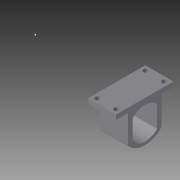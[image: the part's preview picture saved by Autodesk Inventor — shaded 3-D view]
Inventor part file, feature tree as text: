
AUTODESK INVENTOR PART (.ipt)
format: ipt  version: 2015 (Build 190159000, 159)  size: 276,480 bytes
history: native  units: in
note: dims shown in document units (in); Inventor stores cm internally (conversion verified against a paired STEP export)
features: sketch x21, extrude x20, fillet x2, plane x1, pattern_circular x1, mirror x1
ambient origin geometry x8: Origin, YZ Plane, XZ Plane, XY Plane, X Axis, Y Axis, Z Axis, Center Point
bodies: Solid1 (feature_tree)
feature tree (46):
  extrude  "Extrusion1"  Depth=0.1181in
  fillet  "Fillet1"  Radius=0.1969in
  fillet  "Fillet2"  [1 undecoded]
  plane  "Work Plane1"
  extrude  "Extrusion3"  Depth=0.1181in
  pattern_circular  "Circular Pattern1"  Count=4 Angle=360.0deg
  extrude  "Extrusion5"  Depth=0.1181in TaperAngle=0.0deg
  extrude  "Extrusion6"  Depth=0.1181in TaperAngle=0.0deg
  extrude  "Extrusion7"  Depth=0.3937in TaperAngle=0.0deg
  sketch  "Sketch11"  dims[d39=0.1969in d40=0.1181in d41=0.0in]
  extrude  "Extrusion8"  Depth=3.937in TaperAngle=0.0deg
  extrude  "Extrusion9"  Depth=0.1181in TaperAngle=0.0deg
  extrude  "Extrusion10"  Depth=0.5512in
  extrude  "Extrusion11"  Depth=0.7087in
  extrude  "Extrusion12"  Depth=0.3937in
  extrude  "Extrusion13"  Depth=0.1181in TaperAngle=0.0deg
  extrude  "Extrusion14"  Depth=0.0106in TaperAngle=0.0deg
  extrude  "Extrusion16"  Depth=0.1181in TaperAngle=0.0deg
  extrude  "Extrusion17"  Depth=0.2953in
  extrude  "Extrusion18"  Depth=0.1181in
  extrude  "Extrusion19"  Depth=0.1181in
  extrude  "Extrusion21"  Depth=0.1181in
  extrude  "Extrusion22"  Depth=0.2953in TaperAngle=0.0deg
  extrude  "Extrusion23"  [1 undecoded]
  extrude  "Extrusion24"  [1 undecoded]
  mirror  "Mirror1"
  sketch  "Sketch1"  dims[d4=0.1181in d5=0.0in d6=0.1969in d7=0.1969in d8=-0.1969in]
  sketch  "Sketch6"  dims[d17=0.7087in d21=0.1181in]
  sketch  "Sketch8"  dims[d22=0.1181in]
  sketch  "Sketch9"  dims[d24=0.7087in d25=0.0in d26=1.5748in d27=360.0deg]
  sketch  "Sketch10"  dims[d35=0.1969in d36=0.1181in d37=0.0in]
  sketch  "Sketch12"  dims[d42=0.3937in d43=0.0in d44=3.937in d45=0.0in]
  sketch  "Sketch13"  dims[d46=3.937in d47=0.0in d48=3.937in d49=0.0in]
  sketch  "Sketch14"  dims[d50=0.1181in d51=3.937in d52=0.0in]
  sketch  "Sketch17"  dims[d53=0.5118in d54=0.0in d55=0.5512in]
  sketch  "Sketch18"  dims[d56=0.126in d57=0.7087in]
  sketch  "Sketch20"  dims[d58=0.3937in d59=0.3937in]
  sketch  "Sketch22"  dims[d60=0.7087in d61=0.0in d62=0.1181in d63=0.0in]
  sketch  "Sketch24"  dims[d69=0.0118in d70=0.0in d71=0.0106in d72=0.0in]
  sketch  "Sketch25"  dims[d73=0.0012in d74=0.0in d75=0.1181in d76=0.0in]
  sketch  "Sketch26"  dims[d84=1.1811in d85=0.0in d86=0.2953in]
  sketch  "Sketch27"  dims[d87=0.7087in d88=0.0in d89=0.1181in]
  sketch  "Sketch32"  dims[d90=0.1181in d91=0.1181in]
  sketch  "Sketch33"  dims[d92=0.1181in d93=0.1181in]
  sketch  "Sketch34"  dims[d94=0.7087in d95=0.0in d96=0.2953in d97=0.0in]
  sketch  "Sketch35"
note: 3 required parameter values undecoded (feature->parameter linkage not recoverable at this tier; creation-order binding heuristic only, values carry confidence <= 0.55)
